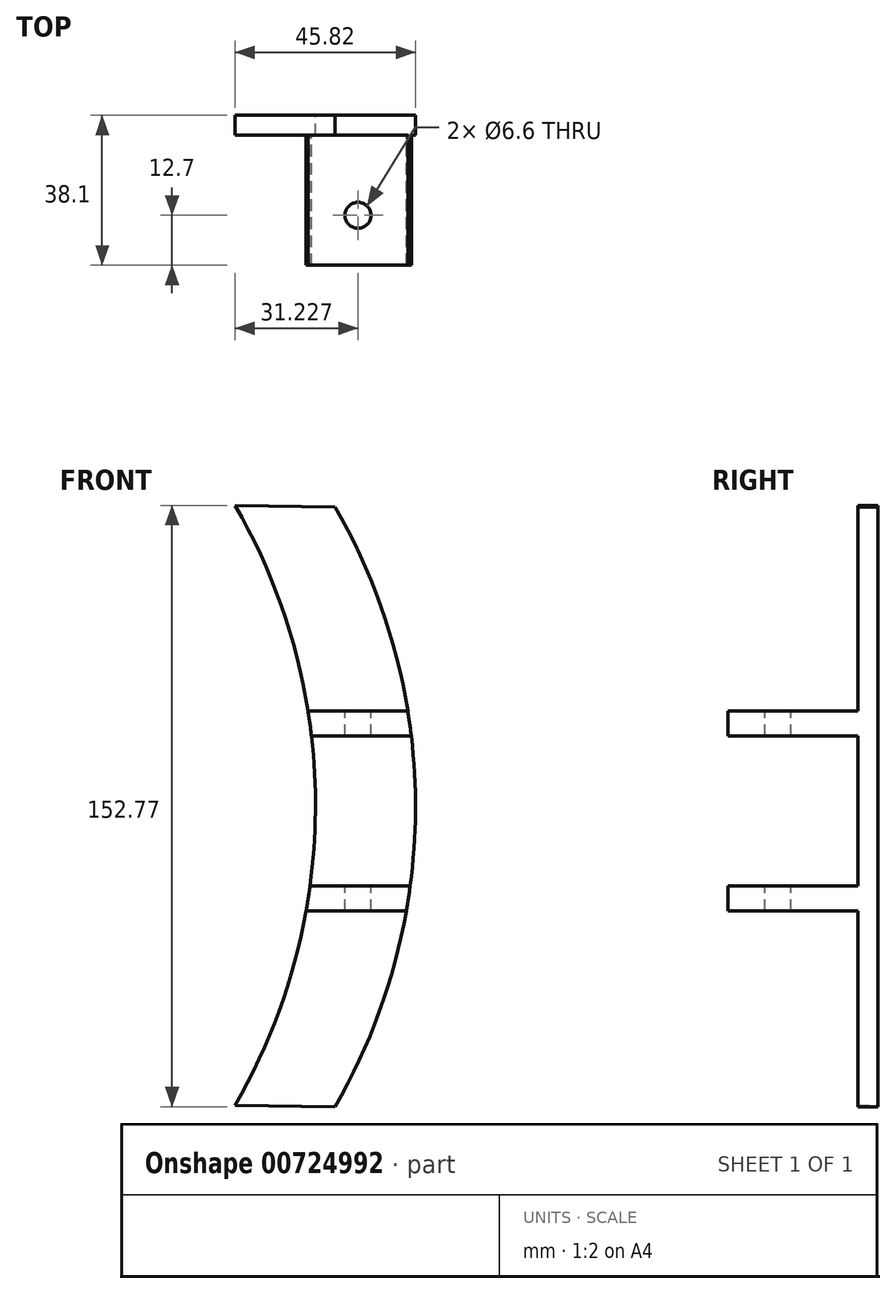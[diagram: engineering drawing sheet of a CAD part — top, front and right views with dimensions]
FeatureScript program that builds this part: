
annotation { "Feature Type Name" : "Feature", "Feature Type Description" : "" }
export const myFeature = defineFeature(function(context is Context, id is Id, definition is map)
    precondition{}
    {
        {
            var Q0;
            Q0=qCreatedBy(makeId("Front.planeOp"),FACE);
            var sketch = newSketch(context, id + "F0", { "sketchPlane" : qUnion([Q0])});
            skArc(sketch, "E0", {"start": v(0, -75.12) * mm, "mid": v(20.42, 1.08) * mm, "end": v(0, 77.28) * mm});
            skArc(sketch, "E1", {"start": v(-25.4, -74.75) * mm, "mid": v(-4.98, 1.45) * mm, "end": v(-25.4, 77.65) * mm});
            skLineSegment(sketch, "E2", {"start": v(-25.4, 77.65) * mm, "end": v(0, 77.28) * mm});
            skLineSegment(sketch, "E3", {"start": v(-25.4, -74.75) * mm, "end": v(0, -75.12) * mm});
            skLineSegment(sketch, "E4", {"start": v(-7.36, -25.4) * mm, "end": v(18.1, -25.4) * mm});
            skLineSegment(sketch, "E5", {"start": v(-6.87, 25.4) * mm, "end": v(18.47, 25.4) * mm});
            skLineSegment(sketch, "E6", {"start": v(-6, 19.05) * mm, "end": v(19.36, 19.05) * mm});
            skLineSegment(sketch, "E7", {"start": v(-6.37, -19.05) * mm, "end": v(19.08, -19.05) * mm});
            skSolve(sketch);
        }
        {
            var Q0;
            Q0 = qSketchRegion(id + "F0", true);
            extrude(context, id + "F1", {"entities" : qUnion([Q0]), "depth" : 5.08 * mm, "offsetDistance" : 25.4 * mm});
        }
        {
            var Q0;
            {var subQ0=sQuery(id+"F0.wireOp",EDGE,"E5");Q0=makeQuery(id+"F0.imprint","IMPRINT",FACE,{"disambiguationData":[TD([[makeQuery(id+"F0.imprint","IMPRINT",EDGE,{"derivedFrom":subQ0}),-1.0]])]});}
            var Q1;
            {var subQ0=sQuery(id+"F0.wireOp",EDGE,"E4");Q1=makeQuery(id+"F0.imprint","IMPRINT",FACE,{"disambiguationData":[TD([[makeQuery(id+"F0.imprint","IMPRINT",EDGE,{"derivedFrom":subQ0}),1.0]])]});}
            extrude(context, id + "F2", {"entities" : qUnion([Q0, Q1]), "operationType" : NewBodyOperationType.ADD, "depth" : 38.1 * mm, "offsetDistance" : 25.4 * mm});
        }
        {
            var Q0;
            Q0=makeQuery(id+"F2.opExtrude","SWEPT_FACE",FACE,{"disambiguationData":[OSD([sQuery(id+"F0.wireOp",EDGE,"E5")])]});
            var sketch = newSketch(context, id + "F3", { "sketchPlane" : qUnion([Q0])});
            skCircle(sketch, "E8", {"center": v(5.83, -25.4) * mm, "radius": 5.08 * mm});
            skSolve(sketch);
        }
        {
            var Q0;
            Q0=sQuery(id+"F3.wireOp",VERTEX,"E8.center");
            var Q1;
            Q1=makeQuery(id+"F1.opExtrude","SWEPT_BODY",BODY,{"disambiguationData":[OSD([sQuery(id+"F0.wireOp",EDGE,"E0"),sQuery(id+"F0.wireOp",EDGE,"E1"),sQuery(id+"F0.wireOp",EDGE,"E2"),sQuery(id+"F0.wireOp",EDGE,"E3")])]});
            hole(context, id + "F4", {"style" : HoleStyle.SIMPLE, "endStyle" : HoleEndStyle.THROUGH, "holeDiameter" : 6.6 * mm, "majorDiameter" : 6.35 * mm, "isTappedThrough" : true, "tappedDepth" : 12.7 * mm, "tapClearance" : 3, "locations" : qUnion([Q0]), "scope" : qUnion([Q1])});
        }
    });
